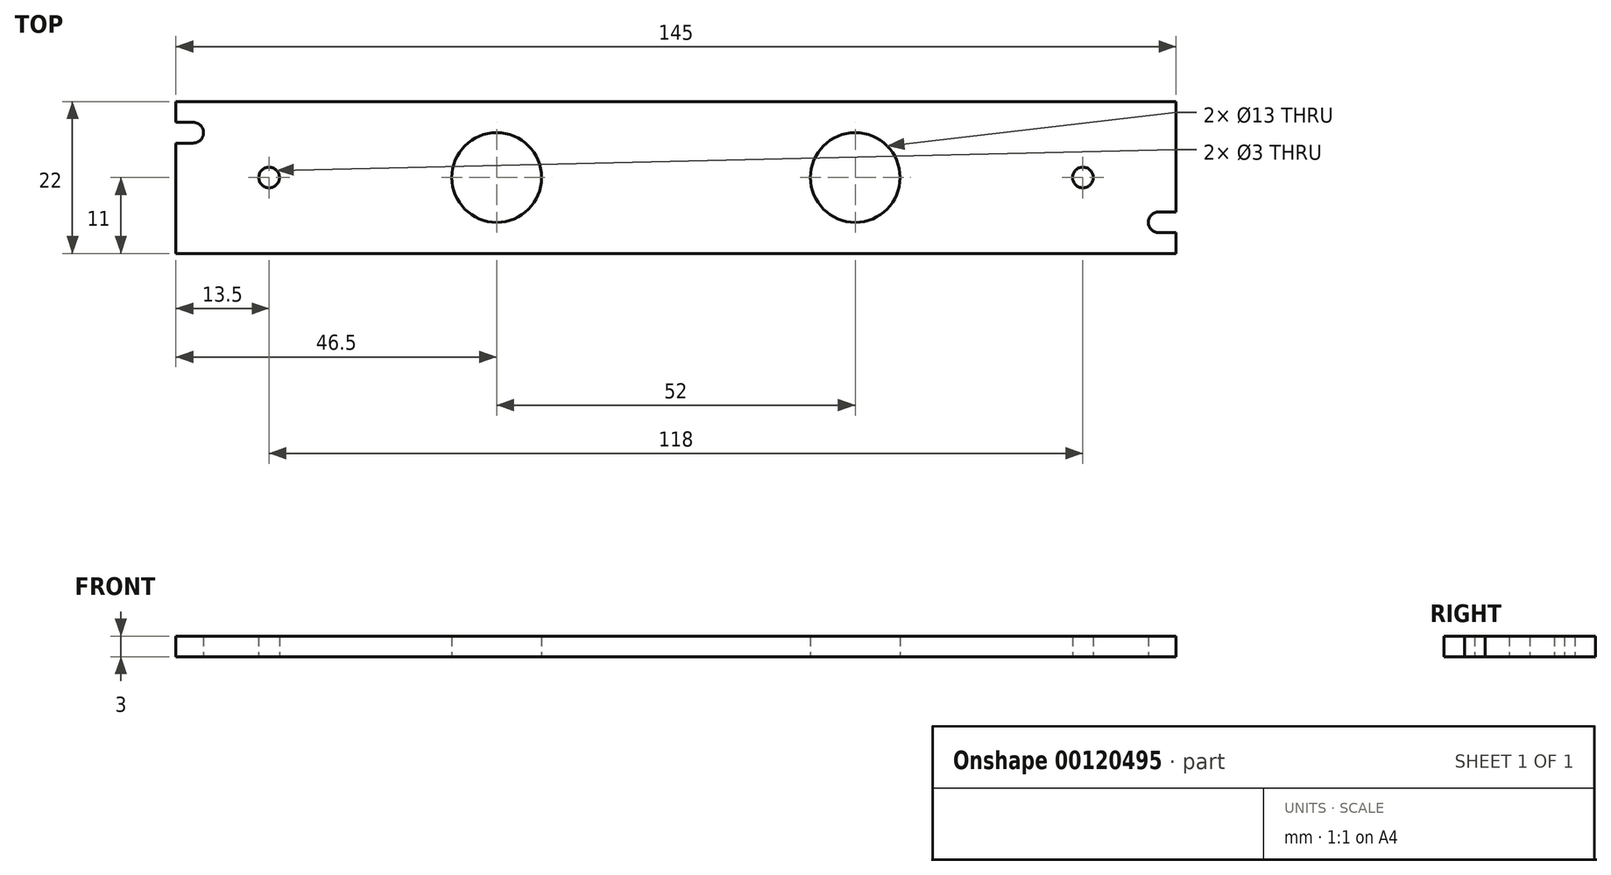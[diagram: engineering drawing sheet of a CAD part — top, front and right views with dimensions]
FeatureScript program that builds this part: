
annotation { "Feature Type Name" : "Feature", "Feature Type Description" : "" }
export const myFeature = defineFeature(function(context is Context, id is Id, definition is map)
    precondition{}
    {
        {
            var Q0;
            Q0=qCreatedBy(makeId("Top.planeOp"),FACE);
            var sketch = newSketch(context, id + "F0", { "sketchPlane" : qUnion([Q0])});
            skLineSegment(sketch, "E0.bottom", {"start": v(0, 0) * mm, "end": v(145, 0) * mm});
            skLineSegment(sketch, "E0.top", {"start": v(0, -22) * mm, "end": v(145, -22) * mm});
            skLineSegment(sketch, "E0.left", {"start": v(0, 0) * mm, "end": v(0, -22) * mm});
            skLineSegment(sketch, "E0.right", {"start": v(145, 0) * mm, "end": v(145, -22) * mm});
            skCircle(sketch, "E1", {"center": v(46.5, -11) * mm, "radius": 6.5 * mm});
            skCircle(sketch, "E2", {"center": v(98.5, -11) * mm, "radius": 6.5 * mm});
            skCircle(sketch, "E3", {"center": v(13.5, -11) * mm, "radius": 1.5 * mm});
            skCircle(sketch, "E4", {"center": v(131.5, -11) * mm, "radius": 1.5 * mm});
            skSolve(sketch);
        }
        {
            var Q0;
            Q0 = qSketchRegion(id + "F0", true);
            extrude(context, id + "F1", {"entities" : qUnion([Q0]), "depth" : 3 * mm});
        }
        {
            var Q0;
            Q0=qCreatedBy(makeId("Top.planeOp"),FACE);
            var sketch = newSketch(context, id + "F2", { "sketchPlane" : qUnion([Q0])});
            skArc(sketch, "E5", {"start": v(2.5, -6) * mm, "mid": v(4, -4.5) * mm, "end": v(2.5, -3) * mm});
            skLineSegment(sketch, "E6", {"start": v(2.5, -3) * mm, "end": v(-2.5, -3) * mm});
            skLineSegment(sketch, "E7", {"start": v(2.5, -6) * mm, "end": v(-2.5, -6) * mm});
            skLineSegment(sketch, "E8", {"start": v(-2.5, -6) * mm, "end": v(-2.5, -3) * mm});
            skArc(sketch, "E9", {"start": v(142.5, -16) * mm, "mid": v(141, -17.5) * mm, "end": v(142.5, -19) * mm});
            skLineSegment(sketch, "E10", {"start": v(142.5, -16) * mm, "end": v(147.5, -16) * mm});
            skLineSegment(sketch, "E11", {"start": v(147.5, -16) * mm, "end": v(147.5, -19) * mm});
            skLineSegment(sketch, "E12", {"start": v(147.5, -19) * mm, "end": v(142.5, -19) * mm});
            skSolve(sketch);
        }
        {
            var Q0;
            Q0 = qSketchRegion(id + "F2", true);
            extrude(context, id + "F3", {"entities" : qUnion([Q0]), "operationType" : NewBodyOperationType.REMOVE, "depth" : 25 * mm});
        }
    });
